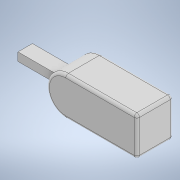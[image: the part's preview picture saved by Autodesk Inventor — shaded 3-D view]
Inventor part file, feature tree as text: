
AUTODESK INVENTOR PART (.ipt)
format: ipt  version: 2020 (Build 240168000, 168)  size: 148,480 bytes
history: native  units: mm
features: extrude x2, fillet x2, sketch x2, other x1
ambient origin geometry x8: Origin, YZ Plane, XZ Plane, XY Plane, X Axis, Y Axis, Z Axis, Center Point
bodies: Body1 (feature_tree)
feature tree (7):
  other  "Твердое тело1"
  extrude  "Выдавливание1"  Depth=28.0mm
  fillet  "Сопряжение1"  Radius=66.0mm
  fillet  "Сопряжение2"  Radius=26.5mm
  extrude  "Выдавливание2"  Depth=2.0mm
  sketch  "Эскиз1"
  sketch  "Эскиз2"
